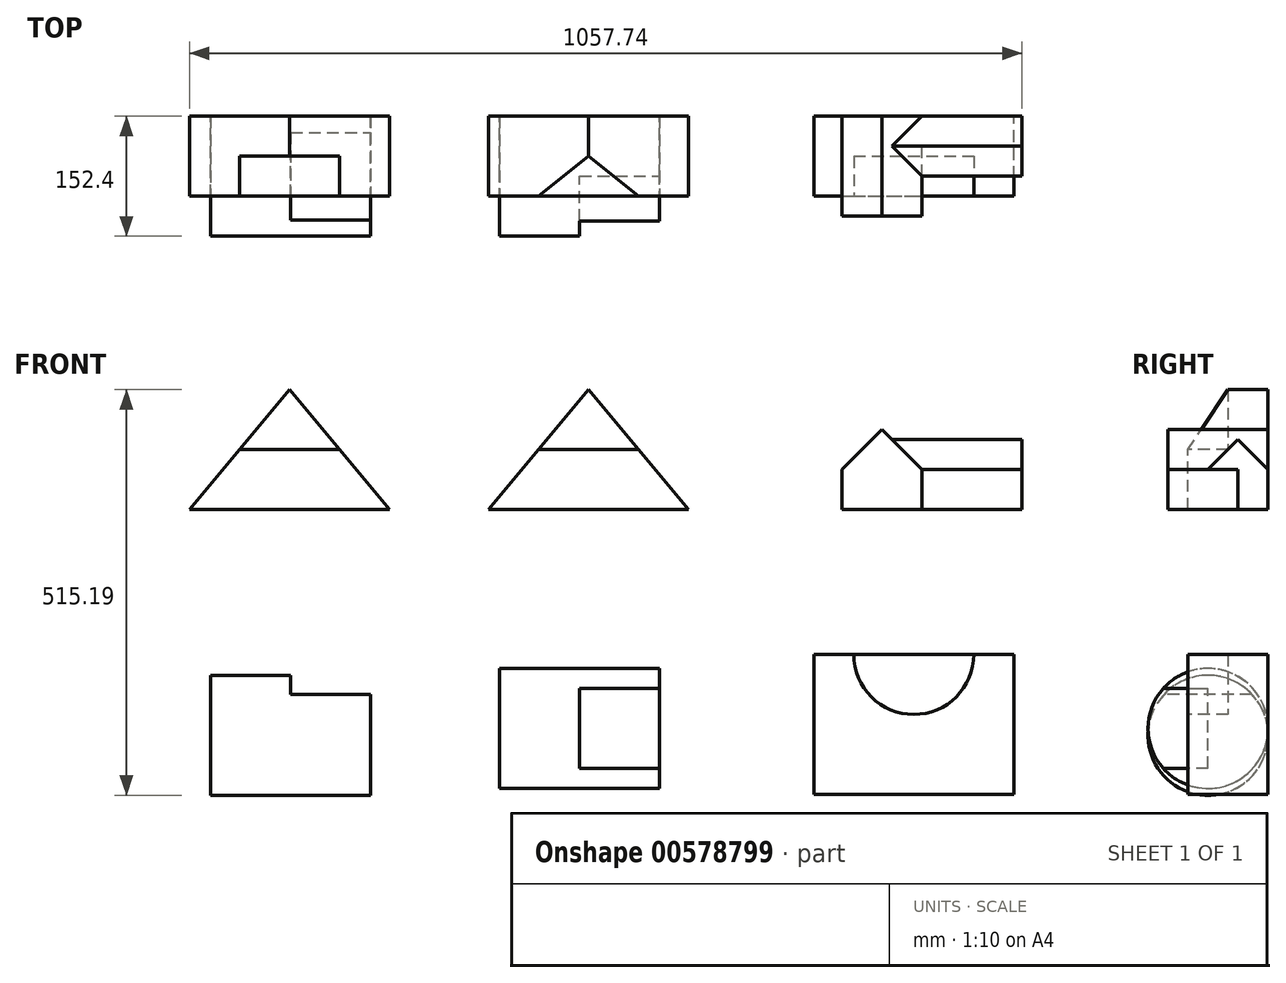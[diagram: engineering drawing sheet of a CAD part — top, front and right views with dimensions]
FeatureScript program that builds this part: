
annotation { "Feature Type Name" : "Feature", "Feature Type Description" : "" }
export const myFeature = defineFeature(function(context is Context, id is Id, definition is map)
    precondition{}
    {
        {
            var Q0;
            Q0=qCreatedBy(makeId("Front.planeOp"),FACE);
            var sketch = newSketch(context, id + "F0", { "sketchPlane" : qUnion([Q0])});
            skLineSegment(sketch, "E0", {"start": v(0, 0) * mm, "end": v(127, 0) * mm});
            skLineSegment(sketch, "E1", {"start": v(-127, 0) * mm, "end": v(0, 0) * mm});
            skLineSegment(sketch, "E2", {"start": v(0, 152.4) * mm, "end": v(-127, 0) * mm});
            skLineSegment(sketch, "E3", {"start": v(0, 152.4) * mm, "end": v(127, 0) * mm});
            skLineSegment(sketch, "E4", {"start": v(0, 76.2) * mm, "end": v(-63.5, 76.2) * mm});
            skLineSegment(sketch, "E5", {"start": v(-63.5, 76.2) * mm, "end": v(63.5, 76.2) * mm});
            skSolve(sketch);
        }
        {
            var Q0;
            {var subQ3=sQuery(id+"F0.wireOp",EDGE,"E5");var subQ6=makeQuery(id+"F0.imprint","IMPRINT",VERTEX,{"derivedFrom":subQ3});Q0=makeQuery(id+"F0.imprint","IMPRINT",FACE,{"disambiguationData":[TD([[makeQuery(id+"F0.imprint","IMPRINT",EDGE,{"disambiguationData":[TD([[subQ6,1.0]])],"derivedFrom":subQ3}),1.0]])]});}
            var Q1;
            {var subQ5=sQuery(id+"F0.wireOp",EDGE,"E0");Q1=makeQuery(id+"F0.imprint","IMPRINT",FACE,{"disambiguationData":[TD([[makeQuery(id+"F0.imprint","IMPRINT",EDGE,{"derivedFrom":subQ5}),1.0]])]});}
            extrude(context, id + "F1", {"entities" : qUnion([Q0, Q1]), "depth" : 101.6 * mm, "offsetDistance" : 25.4 * mm});
        }
        {
            var Q0;
            Q0=makeQuery(id+"F1.opExtrude","CAP_FACE",FACE,{"disambiguationData":[OSD([sQuery(id+"F0.wireOp",EDGE,"E0"),sQuery(id+"F0.wireOp",EDGE,"E1"),sQuery(id+"F0.wireOp",EDGE,"E2"),sQuery(id+"F0.wireOp",EDGE,"E3")])],"isStart":false});
            var sketch = newSketch(context, id + "F2", { "sketchPlane" : qUnion([Q0])});
            skLineSegment(sketch, "E6", {"start": v(0, 76.2) * mm, "end": v(-63.5, 76.2) * mm});
            skLineSegment(sketch, "E7", {"start": v(-63.5, 76.2) * mm, "end": v(63.5, 76.2) * mm});
            skSolve(sketch);
        }
        {
            var Q0;
            {var subQ0=sQuery(id+"F2.wireOp",EDGE,"E7");var subQ3=makeQuery(id+"F2.imprint","IMPRINT",VERTEX,{"derivedFrom":subQ0});Q0=makeQuery(id+"F2.imprint","IMPRINT",FACE,{"disambiguationData":[TD([[makeQuery(id+"F2.imprint","IMPRINT",EDGE,{"disambiguationData":[TD([[subQ3,1.0]])],"derivedFrom":subQ0}),1.0]])]});}
            extrude(context, id + "F3", {"entities" : qUnion([Q0]), "operationType" : NewBodyOperationType.REMOVE, "oppositeDirection" : true, "depth" : 50.8 * mm, "offsetDistance" : 25.4 * mm});
        }
        {
            var Q0;
            Q0=qCreatedBy(makeId("Front.planeOp"),FACE);
            var sketch = newSketch(context, id + "F4", { "sketchPlane" : qUnion([Q0])});
            skLineSegment(sketch, "E8", {"start": v(252.93, 0) * mm, "end": v(506.93, 0) * mm});
            skLineSegment(sketch, "E9", {"start": v(252.93, 0) * mm, "end": v(379.93, 152.4) * mm});
            skLineSegment(sketch, "E10", {"start": v(506.93, 0) * mm, "end": v(379.93, 152.4) * mm});
            skLineSegment(sketch, "E11", {"start": v(316.43, 76.2) * mm, "end": v(443.43, 76.2) * mm});
            skSolve(sketch);
        }
        {
            var Q0;
            {var subQ0=sQuery(id+"F4.wireOp",EDGE,"E8");Q0=makeQuery(id+"F4.imprint","IMPRINT",FACE,{"disambiguationData":[TD([[makeQuery(id+"F4.imprint","IMPRINT",EDGE,{"derivedFrom":subQ0}),1.0]])]});}
            var Q1;
            {var subQ3=sQuery(id+"F4.wireOp",EDGE,"E11");Q1=makeQuery(id+"F4.imprint","IMPRINT",FACE,{"disambiguationData":[TD([[makeQuery(id+"F4.imprint","IMPRINT",EDGE,{"derivedFrom":subQ3}),1.0]])]});}
            extrude(context, id + "F5", {"entities" : qUnion([Q0, Q1]), "depth" : 101.6 * mm, "offsetDistance" : 25.4 * mm});
        }
        {
            var Q0;
            Q0=makeQuery(id+"F5.opExtrude","CAP_EDGE",EDGE,{"disambiguationData":[OSD([sQuery(id+"F4.wireOp",EDGE,"E8")])],"isStart":false});
            cPoint(context, id + "F6", {"entities" : qUnion([Q0]), "parameter" : 0.5});
        }
        {
            var Q0;
            Q0=makeQuery(id+"F5.opExtrude","CAP_VERTEX",VERTEX,{"disambiguationData":[OSD([sQuery(id+"F4.wireOp",EDGE,"E9"),sQuery(id+"F4.wireOp",EDGE,"E10")])],"isStart":false});
            var Q1;
            Q1=makeQuery(id+"F5.opExtrude","CAP_VERTEX",VERTEX,{"disambiguationData":[OSD([sQuery(id+"F4.wireOp",EDGE,"E9"),sQuery(id+"F4.wireOp",EDGE,"E10")])],"isStart":true});
            var Q2;
            Q2 = qCreatedBy(id + "F6" ,VERTEX);
            cPlane(context, id + "F7", {"entities" : qUnion([Q0, Q1, Q2]), "cplaneType" : CPlaneType.THREE_POINT, "offset" : 25.4 * mm, "width" : 152.4 * mm, "height" : 152.4 * mm});
        }
        {
            var Q0;
            Q0=qCreatedBy(id+"F7.planeOp",FACE);
            var sketch = newSketch(context, id + "F8", { "sketchPlane" : qUnion([Q0])});
            skPoint(sketch, "E12.0", {"position": v(-101.6, 152.4) * mm});
            skLineSegment(sketch, "E13.0", {"start": v(-101.6, 152.4) * mm, "end": v(0, 152.4) * mm});
            skPoint(sketch, "E14.0", {"position": v(0, 152.4) * mm});
            skLineSegment(sketch, "E15", {"start": v(-50.8, 152.4) * mm, "end": v(-101.6, 76.2) * mm});
            skLineSegment(sketch, "E16", {"start": v(-101.6, 152.4) * mm, "end": v(-101.6, 76.2) * mm});
            skSolve(sketch);
        }
        {
            var Q0;
            Q0 = qSketchRegion(id + "F8", true);
            extrude(context, id + "F9", {"entities" : qUnion([Q0]), "operationType" : NewBodyOperationType.REMOVE, "endBound" : BoundingType.SYMMETRIC, "oppositeDirection" : true, "depth" : 152.4 * mm, "offsetDistance" : 25.4 * mm});
        }
        {
            var Q0;
            Q0=qCreatedBy(makeId("Front.planeOp"),FACE);
            var sketch = newSketch(context, id + "F10", { "sketchPlane" : qUnion([Q0])});
            skLineSegment(sketch, "E17", {"start": v(702.14, 0) * mm, "end": v(803.74, 0) * mm});
            skLineSegment(sketch, "E18", {"start": v(803.74, 0) * mm, "end": v(803.74, 50.8) * mm});
            skLineSegment(sketch, "E19", {"start": v(702.14, 0) * mm, "end": v(702.14, 50.8) * mm});
            skLineSegment(sketch, "E20", {"start": v(752.94, 0) * mm, "end": v(752.94, 101.6) * mm});
            skLineSegment(sketch, "E21", {"start": v(702.14, 50.8) * mm, "end": v(752.94, 101.6) * mm});
            skLineSegment(sketch, "E22", {"start": v(803.74, 50.8) * mm, "end": v(752.94, 101.6) * mm});
            skSolve(sketch);
        }
        {
            var Q0;
            {var subQ1=sQuery(id+"F10.wireOp",EDGE,"E18");Q0=makeQuery(id+"F10.imprint","IMPRINT",FACE,{"disambiguationData":[TD([[makeQuery(id+"F10.imprint","IMPRINT",EDGE,{"derivedFrom":subQ1}),-1.0]])]});}
            var Q1;
            {var subQ1=sQuery(id+"F10.wireOp",EDGE,"E18");Q1=makeQuery(id+"F10.imprint","IMPRINT",FACE,{"disambiguationData":[TD([[makeQuery(id+"F10.imprint","IMPRINT",EDGE,{"derivedFrom":subQ1}),1.0]])]});}
            var Q2;
            {var subQ0=sQuery(id+"F10.wireOp",EDGE,"E19");Q2=makeQuery(id+"F10.imprint","IMPRINT",FACE,{"disambiguationData":[TD([[makeQuery(id+"F10.imprint","IMPRINT",EDGE,{"derivedFrom":subQ0}),-1.0]])]});}
            extrude(context, id + "F11", {"entities" : qUnion([Q0, Q1, Q2]), "depth" : 127 * mm, "offsetDistance" : 25.4 * mm});
        }
        {
            var Q0;
            Q0=makeQuery(id+"F11.opExtrude","SWEPT_FACE",FACE,{"disambiguationData":[OSD([sQuery(id+"F10.wireOp",EDGE,"E18")])]});
            cPlane(context, id + "F12", {"entities" : qUnion([Q0]), "cplaneType" : CPlaneType.OFFSET, "offset" : 127 * mm, "width" : 152.4 * mm, "height" : 152.4 * mm});
        }
        {
            var Q0;
            Q0=qCreatedBy(id+"F12.planeOp",FACE);
            var sketch = newSketch(context, id + "F13", { "sketchPlane" : qUnion([Q0])});
            skLineSegment(sketch, "E23", {"start": v(0, 0) * mm, "end": v(-76.2, 0) * mm});
            skLineSegment(sketch, "E24", {"start": v(0, 0) * mm, "end": v(0, 50.8) * mm});
            skLineSegment(sketch, "E25", {"start": v(-76.2, 0) * mm, "end": v(-76.2, 50.8) * mm});
            skLineSegment(sketch, "E26", {"start": v(-76.2, 50.8) * mm, "end": v(0, 50.8) * mm});
            skLineSegment(sketch, "E27", {"start": v(-38.1, 0) * mm, "end": v(-38.1, 88.9) * mm});
            skPoint(sketch, "E27.endSnap0", {"position": v(-38.1, 50.8) * mm});
            skLineSegment(sketch, "E28", {"start": v(-76.2, 50.8) * mm, "end": v(-38.1, 88.9) * mm});
            skLineSegment(sketch, "E29", {"start": v(0, 50.8) * mm, "end": v(-38.1, 88.9) * mm});
            skLineSegment(sketch, "E30", {"start": v(-76.2, 50.8) * mm, "end": v(-76.2, 0) * mm});
            skSolve(sketch);
        }
        {
            var Q0;
            {var subQ0=sQuery(id+"F13.wireOp",EDGE,"E28");Q0=makeQuery(id+"F13.imprint","IMPRINT",FACE,{"disambiguationData":[TD([[makeQuery(id+"F13.imprint","IMPRINT",EDGE,{"derivedFrom":subQ0}),-1.0]])]});}
            var Q1;
            {var subQ0=sQuery(id+"F13.wireOp",EDGE,"E29");Q1=makeQuery(id+"F13.imprint","IMPRINT",FACE,{"disambiguationData":[TD([[makeQuery(id+"F13.imprint","IMPRINT",EDGE,{"derivedFrom":subQ0}),1.0]])]});}
            var Q2;
            {var subQ0=sQuery(id+"F13.wireOp",EDGE,"E24");Q2=makeQuery(id+"F13.imprint","IMPRINT",FACE,{"disambiguationData":[TD([[makeQuery(id+"F13.imprint","IMPRINT",EDGE,{"derivedFrom":subQ0}),1.0]])]});}
            var Q3;
            {var subQ0=sQuery(id+"F13.wireOp",EDGE,"E30");Q3=makeQuery(id+"F13.imprint","IMPRINT",FACE,{"disambiguationData":[TD([[makeQuery(id+"F13.imprint","IMPRINT",EDGE,{"derivedFrom":subQ0}),1.0]])]});}
            extrude(context, id + "F14", {"entities" : qUnion([Q0, Q1, Q2, Q3]), "operationType" : NewBodyOperationType.ADD, "oppositeDirection" : true, "depth" : 177.8 * mm, "offsetDistance" : 25.4 * mm});
        }
        {
            var Q0;
            Q0=qCreatedBy(makeId("Front.planeOp"),FACE);
            var sketch = newSketch(context, id + "F15", { "sketchPlane" : qUnion([Q0])});
            skLineSegment(sketch, "E31", {"start": v(-99.83, -362.8) * mm, "end": v(-99.83, -210.4) * mm});
            skLineSegment(sketch, "E32", {"start": v(-99.83, -210.4) * mm, "end": v(103.37, -210.4) * mm});
            skLineSegment(sketch, "E33", {"start": v(103.37, -210.4) * mm, "end": v(103.37, -362.8) * mm});
            skLineSegment(sketch, "E34", {"start": v(103.37, -362.8) * mm, "end": v(-99.83, -362.8) * mm});
            skSolve(sketch);
        }
        {
            var Q0;
            Q0=makeQuery(id+"F15.imprint","IMPRINT",FACE,{"disambiguationData":[TD([[makeQuery(id+"F15.imprint","IMPRINT",EDGE,{"derivedFrom":sQuery(id+"F15.wireOp",EDGE,"E31")}),-1.0]])]});
            extrude(context, id + "F16", {"entities" : qUnion([Q0]), "depth" : 152.4 * mm, "offsetDistance" : 25.4 * mm});
        }
        {
            var Q0;
            Q0=makeQuery(id+"F16.opExtrude","SWEPT_FACE",FACE,{"disambiguationData":[OSD([sQuery(id+"F15.wireOp",EDGE,"E33")])]});
            var sketch = newSketch(context, id + "F17", { "sketchPlane" : qUnion([Q0])});
            skLineSegment(sketch, "E35", {"start": v(-76.2, -210.4) * mm, "end": v(-76.2, -362.8) * mm});
            skLineSegment(sketch, "E36", {"start": v(-152.4, -286.6) * mm, "end": v(0, -286.6) * mm});
            skCircle(sketch, "E37", {"center": v(-76.2, -286.6) * mm, "radius": 76.2 * mm});
            skSolve(sketch);
        }
        {
            var Q0;
            Q0=makeQuery(id+"F16.opExtrude","CAP_FACE",FACE,{"disambiguationData":[OSD([sQuery(id+"F15.wireOp",EDGE,"E31"),sQuery(id+"F15.wireOp",EDGE,"E32"),sQuery(id+"F15.wireOp",EDGE,"E33"),sQuery(id+"F15.wireOp",EDGE,"E34")])],"isStart":false});
            var sketch = newSketch(context, id + "F18", { "sketchPlane" : qUnion([Q0])});
            skLineSegment(sketch, "E38", {"start": v(-99.83, -210.4) * mm, "end": v(1.77, -210.4) * mm});
            skLineSegment(sketch, "E39", {"start": v(1.77, -210.4) * mm, "end": v(1.77, -234.44) * mm});
            skLineSegment(sketch, "E40", {"start": v(1.77, -234.44) * mm, "end": v(103.37, -234.44) * mm});
            skSolve(sketch);
        }
        {
            var Q0;
            {var subQ1=sQuery(id+"F15.wireOp",EDGE,"E33");var subQ2=makeQuery(id+"F16.opExtrude","SWEPT_EDGE",EDGE,{"disambiguationData":[OSD([sQuery(id+"F15.wireOp",EDGE,"E32"),subQ1])]});var subQ4=makeQuery(id+"F16.opExtrude","CAP_EDGE",EDGE,{"disambiguationData":[OSD([subQ1])],"isStart":false});var subQ6=makeQuery(id+"F17.imprint","INTERSECT",VERTEX,{"derivedFrom":[subQ2,subQ4]});Q0=makeQuery(id+"F17.imprint","IMPRINT",FACE,{"disambiguationData":[TD([[makeQuery(id+"F17.imprint","IMPRINT",EDGE,{"disambiguationData":[TD([[subQ6,-1.0]])],"derivedFrom":subQ4}),1.0]])]});}
            var Q1;
            {var subQ1=sQuery(id+"F15.wireOp",EDGE,"E33");var subQ2=makeQuery(id+"F16.opExtrude","SWEPT_EDGE",EDGE,{"disambiguationData":[OSD([sQuery(id+"F15.wireOp",EDGE,"E32"),subQ1])]});var subQ4=makeQuery(id+"F16.opExtrude","CAP_EDGE",EDGE,{"disambiguationData":[OSD([subQ1])],"isStart":true});var subQ6=makeQuery(id+"F17.imprint","INTERSECT",VERTEX,{"derivedFrom":[subQ2,subQ4]});Q1=makeQuery(id+"F17.imprint","IMPRINT",FACE,{"disambiguationData":[TD([[makeQuery(id+"F17.imprint","IMPRINT",EDGE,{"disambiguationData":[TD([[subQ6,-1.0]])],"derivedFrom":subQ4}),-1.0]])]});}
            var Q2;
            {var subQ1=sQuery(id+"F15.wireOp",EDGE,"E33");var subQ2=makeQuery(id+"F16.opExtrude","SWEPT_EDGE",EDGE,{"disambiguationData":[OSD([subQ1,sQuery(id+"F15.wireOp",EDGE,"E34")])]});var subQ4=makeQuery(id+"F16.opExtrude","CAP_EDGE",EDGE,{"disambiguationData":[OSD([subQ1])],"isStart":true});var subQ6=makeQuery(id+"F17.imprint","INTERSECT",VERTEX,{"derivedFrom":[subQ2,subQ4]});Q2=makeQuery(id+"F17.imprint","IMPRINT",FACE,{"disambiguationData":[TD([[makeQuery(id+"F17.imprint","IMPRINT",EDGE,{"disambiguationData":[TD([[subQ6,1.0]])],"derivedFrom":subQ4}),-1.0]])]});}
            var Q3;
            {var subQ1=sQuery(id+"F15.wireOp",EDGE,"E33");var subQ2=makeQuery(id+"F16.opExtrude","SWEPT_EDGE",EDGE,{"disambiguationData":[OSD([subQ1,sQuery(id+"F15.wireOp",EDGE,"E34")])]});var subQ4=makeQuery(id+"F16.opExtrude","CAP_EDGE",EDGE,{"disambiguationData":[OSD([subQ1])],"isStart":false});var subQ6=makeQuery(id+"F17.imprint","INTERSECT",VERTEX,{"derivedFrom":[subQ2,subQ4]});Q3=makeQuery(id+"F17.imprint","IMPRINT",FACE,{"disambiguationData":[TD([[makeQuery(id+"F17.imprint","IMPRINT",EDGE,{"disambiguationData":[TD([[subQ6,1.0]])],"derivedFrom":subQ4}),1.0]])]});}
            extrude(context, id + "F19", {"entities" : qUnion([Q0, Q1, Q2, Q3]), "operationType" : NewBodyOperationType.REMOVE, "oppositeDirection" : true, "depth" : 360.68 * mm, "offsetDistance" : 25.4 * mm});
        }
        {
            var Q0;
            {var subQ0=sQuery(id+"F18.wireOp",EDGE,"E39");Q0=makeQuery(id+"F18.imprint","IMPRINT",FACE,{"disambiguationData":[TD([[makeQuery(id+"F18.imprint","IMPRINT",EDGE,{"derivedFrom":subQ0}),1.0]])]});}
            extrude(context, id + "F20", {"entities" : qUnion([Q0]), "operationType" : NewBodyOperationType.REMOVE, "oppositeDirection" : true, "depth" : 185.42 * mm, "offsetDistance" : 25.4 * mm});
        }
        {
            var Q0;
            Q0=qCreatedBy(makeId("Front.planeOp"),FACE);
            var sketch = newSketch(context, id + "F21", { "sketchPlane" : qUnion([Q0])});
            skLineSegment(sketch, "E41.bottom", {"start": v(267.03, -354.11) * mm, "end": v(470.23, -354.11) * mm});
            skLineSegment(sketch, "E41.top", {"start": v(267.03, -201.71) * mm, "end": v(470.23, -201.71) * mm});
            skLineSegment(sketch, "E41.left", {"start": v(267.03, -354.11) * mm, "end": v(267.03, -201.71) * mm});
            skLineSegment(sketch, "E41.right", {"start": v(470.23, -354.11) * mm, "end": v(470.23, -201.71) * mm});
            skSolve(sketch);
        }
        {
            var Q0;
            Q0=makeQuery(id+"F21.imprint","IMPRINT",FACE,{"disambiguationData":[TD([[makeQuery(id+"F21.imprint","IMPRINT",EDGE,{"derivedFrom":sQuery(id+"F21.wireOp",EDGE,"E41.bottom")}),1.0]])]});
            extrude(context, id + "F22", {"entities" : qUnion([Q0]), "depth" : 152.4 * mm, "offsetDistance" : 25.4 * mm});
        }
        {
            var Q0;
            Q0=makeQuery(id+"F22.opExtrude","SWEPT_FACE",FACE,{"disambiguationData":[OSD([sQuery(id+"F21.wireOp",EDGE,"E41.right")])]});
            var sketch = newSketch(context, id + "F23", { "sketchPlane" : qUnion([Q0])});
            skLineSegment(sketch, "E42", {"start": v(-76.2, -354.11) * mm, "end": v(-76.2, -201.71) * mm});
            skLineSegment(sketch, "E43", {"start": v(-152.4, -277.91) * mm, "end": v(0, -277.91) * mm});
            skCircle(sketch, "E44", {"center": v(-76.2, -277.91) * mm, "radius": 76.2 * mm});
            skSolve(sketch);
        }
        {
            var Q0;
            {var subQ1=sQuery(id+"F23.wireOp",EDGE,"E42");var subQ4=sQuery(id+"F23.wireOp",EDGE,"E43");var subQ5=makeQuery(id+"F23.imprint","INTERSECT",VERTEX,{"derivedFrom":[subQ1,subQ4]});Q0=makeQuery(id+"F23.imprint","IMPRINT",FACE,{"disambiguationData":[TD([[makeQuery(id+"F23.imprint","IMPRINT",EDGE,{"disambiguationData":[TD([[subQ5,1.0]])],"derivedFrom":subQ4}),1.0]])]});}
            var sketch = newSketch(context, id + "F24", { "sketchPlane" : qUnion([Q0])});
            skLineSegment(sketch, "E45.0", {"start": v(-152.4, -201.71) * mm, "end": v(0, -201.71) * mm});
            skLineSegment(sketch, "E46.0", {"start": v(-152.4, -354.11) * mm, "end": v(-152.4, -201.71) * mm});
            skLineSegment(sketch, "E47.0", {"start": v(-152.4, -354.11) * mm, "end": v(0, -354.11) * mm});
            skLineSegment(sketch, "E48.0", {"start": v(0, -354.11) * mm, "end": v(0, -201.71) * mm});
            skCircle(sketch, "E49.0", {"center": v(-76.2, -277.91) * mm, "radius": 76.2 * mm});
            skLineSegment(sketch, "E50", {"start": v(-152.4, -277.91) * mm, "end": v(-152.4, -227.11) * mm});
            skLineSegment(sketch, "E51", {"start": v(-152.4, -227.11) * mm, "end": v(-76.2, -227.11) * mm});
            skLineSegment(sketch, "E52", {"start": v(-76.2, -227.11) * mm, "end": v(-76.2, -277.91) * mm});
            skLineSegment(sketch, "E53", {"start": v(-76.2, -277.91) * mm, "end": v(-76.2, -328.71) * mm});
            skLineSegment(sketch, "E54", {"start": v(-76.2, -328.71) * mm, "end": v(-152.4, -328.71) * mm});
            skSolve(sketch);
        }
        {
            var Q0;
            {var subQ1=sQuery(id+"F21.wireOp",EDGE,"E41.right");var subQ2=makeQuery(id+"F22.opExtrude","SWEPT_EDGE",EDGE,{"disambiguationData":[OSD([sQuery(id+"F21.wireOp",EDGE,"E41.top"),subQ1])]});var subQ4=makeQuery(id+"F22.opExtrude","CAP_EDGE",EDGE,{"disambiguationData":[OSD([subQ1])],"isStart":false});var subQ6=makeQuery(id+"F23.imprint","INTERSECT",VERTEX,{"derivedFrom":[subQ2,subQ4]});Q0=makeQuery(id+"F23.imprint","IMPRINT",FACE,{"disambiguationData":[TD([[makeQuery(id+"F23.imprint","IMPRINT",EDGE,{"disambiguationData":[TD([[subQ6,1.0]])],"derivedFrom":subQ4}),-1.0]])]});}
            var Q1;
            {var subQ1=sQuery(id+"F21.wireOp",EDGE,"E41.right");var subQ2=makeQuery(id+"F22.opExtrude","SWEPT_EDGE",EDGE,{"disambiguationData":[OSD([sQuery(id+"F21.wireOp",EDGE,"E41.top"),subQ1])]});var subQ4=makeQuery(id+"F22.opExtrude","CAP_EDGE",EDGE,{"disambiguationData":[OSD([subQ1])],"isStart":true});var subQ6=makeQuery(id+"F23.imprint","INTERSECT",VERTEX,{"derivedFrom":[subQ2,subQ4]});Q1=makeQuery(id+"F23.imprint","IMPRINT",FACE,{"disambiguationData":[TD([[makeQuery(id+"F23.imprint","IMPRINT",EDGE,{"disambiguationData":[TD([[subQ6,1.0]])],"derivedFrom":subQ4}),1.0]])]});}
            var Q2;
            {var subQ1=sQuery(id+"F21.wireOp",EDGE,"E41.right");var subQ2=makeQuery(id+"F22.opExtrude","SWEPT_EDGE",EDGE,{"disambiguationData":[OSD([sQuery(id+"F21.wireOp",EDGE,"E41.bottom"),subQ1])]});var subQ4=makeQuery(id+"F22.opExtrude","CAP_EDGE",EDGE,{"disambiguationData":[OSD([subQ1])],"isStart":true});var subQ6=makeQuery(id+"F23.imprint","INTERSECT",VERTEX,{"derivedFrom":[subQ2,subQ4]});Q2=makeQuery(id+"F23.imprint","IMPRINT",FACE,{"disambiguationData":[TD([[makeQuery(id+"F23.imprint","IMPRINT",EDGE,{"disambiguationData":[TD([[subQ6,-1.0]])],"derivedFrom":subQ4}),1.0]])]});}
            var Q3;
            {var subQ1=sQuery(id+"F21.wireOp",EDGE,"E41.right");var subQ2=makeQuery(id+"F22.opExtrude","SWEPT_EDGE",EDGE,{"disambiguationData":[OSD([sQuery(id+"F21.wireOp",EDGE,"E41.bottom"),subQ1])]});var subQ4=makeQuery(id+"F22.opExtrude","CAP_EDGE",EDGE,{"disambiguationData":[OSD([subQ1])],"isStart":false});var subQ6=makeQuery(id+"F23.imprint","INTERSECT",VERTEX,{"derivedFrom":[subQ2,subQ4]});Q3=makeQuery(id+"F23.imprint","IMPRINT",FACE,{"disambiguationData":[TD([[makeQuery(id+"F23.imprint","IMPRINT",EDGE,{"disambiguationData":[TD([[subQ6,-1.0]])],"derivedFrom":subQ4}),-1.0]])]});}
            extrude(context, id + "F25", {"entities" : qUnion([Q0, Q1, Q2, Q3]), "operationType" : NewBodyOperationType.REMOVE, "oppositeDirection" : true, "depth" : 203.2 * mm, "offsetDistance" : 25.4 * mm});
        }
        {
            var Q0;
            {var subQ9=sQuery(id+"F24.wireOp",EDGE,"E52");Q0=makeQuery(id+"F24.imprint","IMPRINT",FACE,{"disambiguationData":[TD([[makeQuery(id+"F24.imprint","IMPRINT",EDGE,{"derivedFrom":subQ9}),1.0]])]});}
            var Q1;
            {var subQ5=sQuery(id+"F24.wireOp",EDGE,"E53");Q1=makeQuery(id+"F24.imprint","IMPRINT",FACE,{"disambiguationData":[TD([[makeQuery(id+"F24.imprint","IMPRINT",EDGE,{"derivedFrom":subQ5}),-1.0]])]});}
            extrude(context, id + "F26", {"entities" : qUnion([Q0, Q1]), "operationType" : NewBodyOperationType.REMOVE, "oppositeDirection" : true, "depth" : 101.6 * mm, "offsetDistance" : 25.4 * mm});
        }
        {
            var Q0;
            Q0=qCreatedBy(makeId("Front.planeOp"),FACE);
            var sketch = newSketch(context, id + "F27", { "sketchPlane" : qUnion([Q0])});
            skLineSegment(sketch, "E55.bottom", {"start": v(666.19, -361.73) * mm, "end": v(920.19, -361.73) * mm});
            skLineSegment(sketch, "E55.top", {"start": v(666.19, -183.93) * mm, "end": v(920.19, -183.93) * mm});
            skLineSegment(sketch, "E55.left", {"start": v(666.19, -361.73) * mm, "end": v(666.19, -183.93) * mm});
            skLineSegment(sketch, "E55.right", {"start": v(920.19, -361.73) * mm, "end": v(920.19, -183.93) * mm});
            skSolve(sketch);
        }
        {
            var Q0;
            Q0=makeQuery(id+"F27.imprint","IMPRINT",FACE,{"disambiguationData":[TD([[makeQuery(id+"F27.imprint","IMPRINT",EDGE,{"derivedFrom":sQuery(id+"F27.wireOp",EDGE,"E55.bottom")}),1.0]])]});
            extrude(context, id + "F28", {"entities" : qUnion([Q0]), "depth" : 101.6 * mm, "offsetDistance" : 25.4 * mm});
        }
        {
            var Q0;
            Q0=makeQuery(id+"F28.opExtrude","CAP_FACE",FACE,{"disambiguationData":[OSD([sQuery(id+"F27.wireOp",EDGE,"E55.bottom"),sQuery(id+"F27.wireOp",EDGE,"E55.top"),sQuery(id+"F27.wireOp",EDGE,"E55.left"),sQuery(id+"F27.wireOp",EDGE,"E55.right")])],"isStart":false});
            var sketch = newSketch(context, id + "F29", { "sketchPlane" : qUnion([Q0])});
            skLineSegment(sketch, "E56", {"start": v(793.19, -183.93) * mm, "end": v(793.19, -361.73) * mm});
            skCircle(sketch, "E57", {"center": v(793.19, -183.93) * mm, "radius": 76.2 * mm});
            skSolve(sketch);
        }
        {
            var Q0;
            {var subQ0=sQuery(id+"F29.wireOp",EDGE,"E56");var subQ1=makeQuery(id+"F28.opExtrude","CAP_EDGE",EDGE,{"disambiguationData":[OSD([sQuery(id+"F27.wireOp",EDGE,"E55.top")])],"isStart":false});var subQ2=makeQuery(id+"F29.imprint","INTERSECT",VERTEX,{"derivedFrom":[subQ1,subQ0]});Q0=makeQuery(id+"F29.imprint","IMPRINT",FACE,{"disambiguationData":[TD([[makeQuery(id+"F29.imprint","IMPRINT",EDGE,{"disambiguationData":[TD([[subQ2,-1.0]])],"derivedFrom":subQ0}),-1.0]])]});}
            var Q1;
            {var subQ0=sQuery(id+"F29.wireOp",EDGE,"E56");var subQ1=makeQuery(id+"F28.opExtrude","CAP_EDGE",EDGE,{"disambiguationData":[OSD([sQuery(id+"F27.wireOp",EDGE,"E55.top")])],"isStart":false});var subQ2=makeQuery(id+"F29.imprint","INTERSECT",VERTEX,{"derivedFrom":[subQ1,subQ0]});Q1=makeQuery(id+"F29.imprint","IMPRINT",FACE,{"disambiguationData":[TD([[makeQuery(id+"F29.imprint","IMPRINT",EDGE,{"disambiguationData":[TD([[subQ2,-1.0]])],"derivedFrom":subQ0}),1.0]])]});}
            extrude(context, id + "F30", {"entities" : qUnion([Q0, Q1]), "operationType" : NewBodyOperationType.REMOVE, "oppositeDirection" : true, "depth" : 50.8 * mm, "offsetDistance" : 25.4 * mm});
        }
    });
